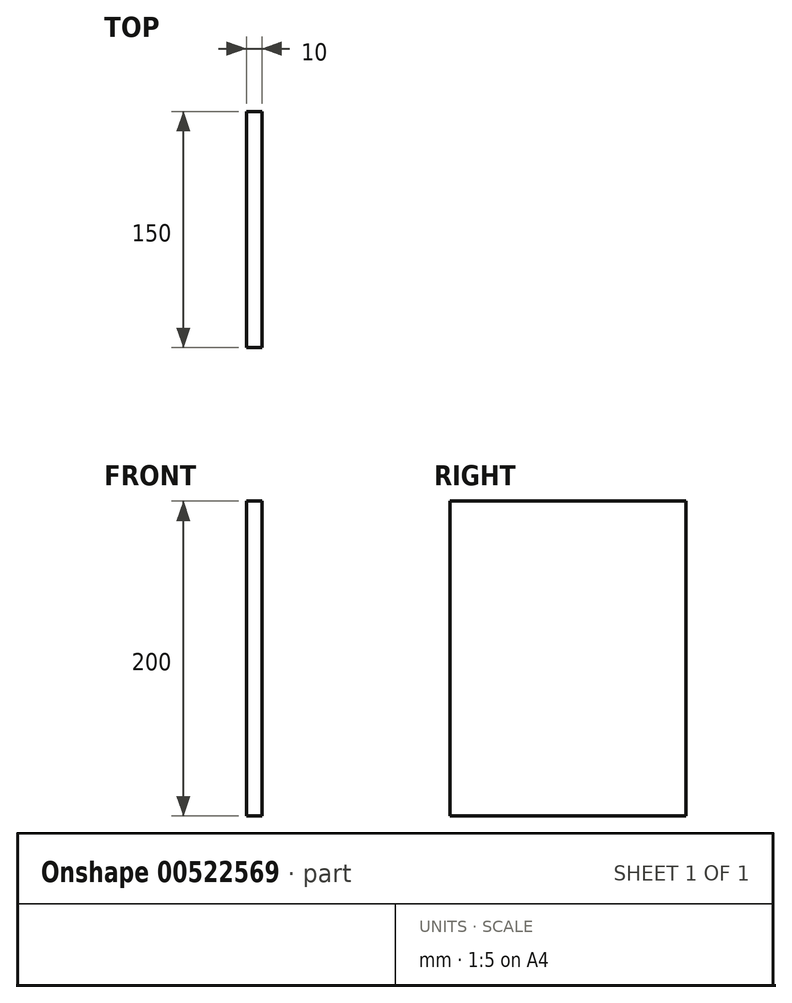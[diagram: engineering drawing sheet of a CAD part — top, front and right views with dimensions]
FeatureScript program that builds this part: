
annotation { "Feature Type Name" : "Feature", "Feature Type Description" : "" }
export const myFeature = defineFeature(function(context is Context, id is Id, definition is map)
    precondition{}
    {
        {
            var Q0;
            Q0=qCreatedBy(makeId("Right.planeOp"),FACE);
            var sketch = newSketch(context, id + "F0", { "sketchPlane" : qUnion([Q0])});
            skLineSegment(sketch, "E0.bottom", {"start": v(-75, 100) * mm, "end": v(75, 100) * mm});
            skLineSegment(sketch, "E0.top", {"start": v(-75, -100) * mm, "end": v(75, -100) * mm});
            skLineSegment(sketch, "E0.left", {"start": v(-75, 100) * mm, "end": v(-75, -100) * mm});
            skLineSegment(sketch, "E0.right", {"start": v(75, 100) * mm, "end": v(75, -100) * mm});
            skPoint(sketch, "E0.middle", {"position": v(0, 0) * mm});
            skSolve(sketch);
        }
        {
            var Q0;
            Q0=makeQuery(id+"F0.imprint","IMPRINT",FACE,{"disambiguationData":[TD([[makeQuery(id+"F0.imprint","IMPRINT",EDGE,{"derivedFrom":sQuery(id+"F0.wireOp",EDGE,"E0.bottom")}),-1.0]])]});
            extrude(context, id + "F1", {"entities" : qUnion([Q0]), "depth" : 10 * mm, "offsetDistance" : 25 * mm});
        }
    });
